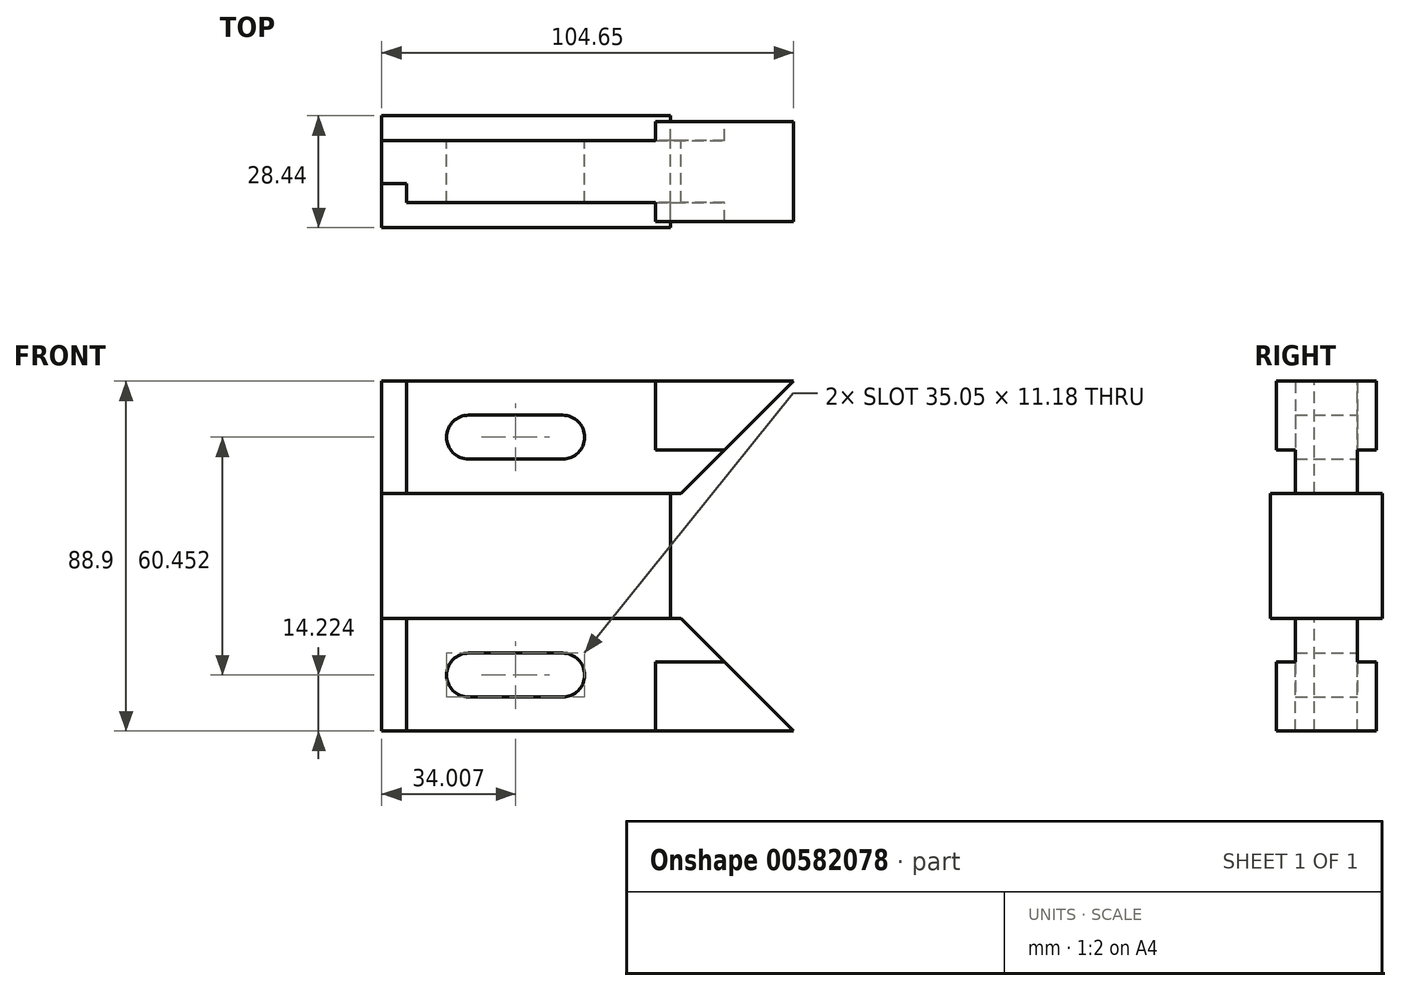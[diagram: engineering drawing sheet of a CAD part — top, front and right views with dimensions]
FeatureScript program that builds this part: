
annotation { "Feature Type Name" : "Feature", "Feature Type Description" : "" }
export const myFeature = defineFeature(function(context is Context, id is Id, definition is map)
    precondition{}
    {
        {
            var Q0;
            Q0=qCreatedBy(makeId("Front.planeOp"),FACE);
            var sketch = newSketch(context, id + "F0", { "sketchPlane" : qUnion([Q0])});
            skLineSegment(sketch, "E0", {"start": v(0, 0) * mm, "end": v(104.65, 0) * mm});
            skLineSegment(sketch, "E1", {"start": v(0, 0) * mm, "end": v(0, 88.9) * mm});
            skLineSegment(sketch, "E2", {"start": v(0, 28.58) * mm, "end": v(73.4, 28.58) * mm});
            skLineSegment(sketch, "E3", {"start": v(0, 60.33) * mm, "end": v(73.4, 60.33) * mm});
            skLineSegment(sketch, "E4", {"start": v(73.4, 60.33) * mm, "end": v(73.4, 28.58) * mm});
            skLineSegment(sketch, "E5", {"start": v(0, 88.9) * mm, "end": v(104.65, 88.9) * mm});
            skLineSegment(sketch, "E6", {"start": v(6.35, 88.9) * mm, "end": v(6.35, 60.33) * mm});
            skLineSegment(sketch, "E7", {"start": v(6.35, 0) * mm, "end": v(6.35, 28.58) * mm});
            skLineSegment(sketch, "E8", {"start": v(104.65, 0) * mm, "end": v(76.07, 28.58) * mm});
            skLineSegment(sketch, "E9", {"start": v(76.07, 28.58) * mm, "end": v(73.4, 28.58) * mm});
            skLineSegment(sketch, "E10", {"start": v(104.65, 88.9) * mm, "end": v(76.07, 60.32) * mm});
            skLineSegment(sketch, "E11", {"start": v(76.07, 60.33) * mm, "end": v(73.4, 60.33) * mm});
            skLineSegment(sketch, "E12", {"start": v(69.6, 88.9) * mm, "end": v(69.6, 71.37) * mm});
            skLineSegment(sketch, "E13", {"start": v(69.6, 71.37) * mm, "end": v(87.12, 71.37) * mm});
            skLineSegment(sketch, "E14", {"start": v(69.6, 0) * mm, "end": v(69.6, 17.53) * mm});
            skLineSegment(sketch, "E15", {"start": v(69.6, 17.53) * mm, "end": v(87.12, 17.53) * mm});
            skArc(sketch, "E16", {"start": v(22.07, 19.81) * mm, "mid": v(16.48, 14.22) * mm, "end": v(22.07, 8.64) * mm});
            skArc(sketch, "E17", {"start": v(45.95, 8.64) * mm, "mid": v(51.53, 14.22) * mm, "end": v(45.95, 19.81) * mm});
            skLineSegment(sketch, "E18", {"start": v(22.07, 19.81) * mm, "end": v(45.95, 19.81) * mm});
            skLineSegment(sketch, "E19", {"start": v(45.95, 8.64) * mm, "end": v(22.07, 8.64) * mm});
            skLineSegment(sketch, "E20", {"start": v(0, 44.45) * mm, "end": v(73.4, 44.45) * mm, "construction": true});
            skArc(sketch, "E21.MirrorCS", {"start": v(22.07, 69.09) * mm, "mid": v(16.48, 74.68) * mm, "end": v(22.07, 80.26) * mm});
            skLineSegment(sketch, "E22.MirrorCS", {"start": v(22.07, 69.09) * mm, "end": v(45.95, 69.09) * mm});
            skLineSegment(sketch, "E23.MirrorCS", {"start": v(45.95, 80.26) * mm, "end": v(22.07, 80.26) * mm});
            skArc(sketch, "E24.MirrorCS", {"start": v(45.95, 80.26) * mm, "mid": v(51.53, 74.68) * mm, "end": v(45.95, 69.09) * mm});
            skSolve(sketch);
        }
        {
            var Q0;
            {var subQ4=sQuery(id+"F0.wireOp",EDGE,"E4");Q0=makeQuery(id+"F0.imprint","IMPRINT",FACE,{"disambiguationData":[TD([[makeQuery(id+"F0.imprint","IMPRINT",EDGE,{"derivedFrom":subQ4}),-1.0]])]});}
            extrude(context, id + "F1", {"entities" : qUnion([Q0]), "endBound" : BoundingType.SYMMETRIC, "depth" : 28.45 * mm, "offsetDistance" : 25.4 * mm});
        }
        {
            var Q0;
            {var subQ3=sQuery(id+"F0.wireOp",EDGE,"E6");Q0=makeQuery(id+"F0.imprint","IMPRINT",FACE,{"disambiguationData":[TD([[makeQuery(id+"F0.imprint","IMPRINT",EDGE,{"derivedFrom":subQ3}),1.0]])]});}
            var Q1;
            {var subQ2=sQuery(id+"F0.wireOp",EDGE,"E7");Q1=makeQuery(id+"F0.imprint","IMPRINT",FACE,{"disambiguationData":[TD([[makeQuery(id+"F0.imprint","IMPRINT",EDGE,{"derivedFrom":subQ2}),-1.0]])]});}
            var Q2;
            {var subQ5=sQuery(id+"F0.wireOp",EDGE,"E6");Q2=makeQuery(id+"F0.imprint","IMPRINT",FACE,{"disambiguationData":[TD([[makeQuery(id+"F0.imprint","IMPRINT",EDGE,{"derivedFrom":subQ5}),-1.0]])]});}
            var Q3;
            {var subQ3=sQuery(id+"F0.wireOp",EDGE,"E7");Q3=makeQuery(id+"F0.imprint","IMPRINT",FACE,{"disambiguationData":[TD([[makeQuery(id+"F0.imprint","IMPRINT",EDGE,{"derivedFrom":subQ3}),1.0]])]});}
            extrude(context, id + "F2", {"entities" : qUnion([Q0, Q1, Q2, Q3]), "operationType" : NewBodyOperationType.ADD, "endBound" : BoundingType.SYMMETRIC, "depth" : 15.75 * mm, "offsetDistance" : 25.4 * mm});
        }
        {
            var Q0;
            {var subQ3=sQuery(id+"F0.wireOp",EDGE,"E12");Q0=makeQuery(id+"F0.imprint","IMPRINT",FACE,{"disambiguationData":[TD([[makeQuery(id+"F0.imprint","IMPRINT",EDGE,{"derivedFrom":subQ3}),1.0]])]});}
            var Q1;
            {var subQ3=sQuery(id+"F0.wireOp",EDGE,"E14");Q1=makeQuery(id+"F0.imprint","IMPRINT",FACE,{"disambiguationData":[TD([[makeQuery(id+"F0.imprint","IMPRINT",EDGE,{"derivedFrom":subQ3}),-1.0]])]});}
            extrude(context, id + "F3", {"entities" : qUnion([Q0, Q1]), "operationType" : NewBodyOperationType.ADD, "endBound" : BoundingType.SYMMETRIC, "depth" : 25.4 * mm, "offsetDistance" : 25.4 * mm});
        }
        {
            var Q0;
            Q0=makeQuery(id+"F2.opExtrude","CAP_FACE",FACE,{"disambiguationData":[OSD([sQuery(id+"F0.wireOp",EDGE,"E1"),sQuery(id+"F0.wireOp",EDGE,"E3"),sQuery(id+"F0.wireOp",EDGE,"E5"),sQuery(id+"F0.wireOp",EDGE,"E10"),sQuery(id+"F0.wireOp",EDGE,"E11"),sQuery(id+"F0.wireOp",EDGE,"E12"),sQuery(id+"F0.wireOp",EDGE,"E13"),sQuery(id+"F0.wireOp",EDGE,"E21.MirrorCS"),sQuery(id+"F0.wireOp",EDGE,"E22.MirrorCS"),sQuery(id+"F0.wireOp",EDGE,"E23.MirrorCS"),sQuery(id+"F0.wireOp",EDGE,"E24.MirrorCS")])],"isStart":false});
            var sketch = newSketch(context, id + "F4", { "sketchPlane" : qUnion([Q0])});
            skLineSegment(sketch, "E25.0", {"start": v(6.35, 88.9) * mm, "end": v(6.35, 60.33) * mm});
            skLineSegment(sketch, "E26.0", {"start": v(0, 0) * mm, "end": v(0, 88.9) * mm});
            skLineSegment(sketch, "E27.0", {"start": v(6.35, 0) * mm, "end": v(6.35, 28.58) * mm});
            skLineSegment(sketch, "E28.0", {"start": v(0, 0) * mm, "end": v(6.35, 0) * mm});
            skLineSegment(sketch, "E29.0", {"start": v(0, 28.58) * mm, "end": v(6.35, 28.58) * mm});
            skLineSegment(sketch, "E30.0", {"start": v(0, 88.9) * mm, "end": v(6.35, 88.9) * mm});
            skPoint(sketch, "E31.orphan", {"position": v(104.65, 88.9) * mm});
            skPoint(sketch, "E32.orphan", {"position": v(69.6, 0) * mm});
            skPoint(sketch, "E33.orphan", {"position": v(73.4, 28.58) * mm});
            skLineSegment(sketch, "E34.0", {"start": v(6.35, 60.32) * mm, "end": v(0, 60.32) * mm});
            skPoint(sketch, "E35.orphan", {"position": v(73.4, 60.33) * mm});
            skSolve(sketch);
        }
        {
            var Q0;
            Q0=makeQuery(id+"F4.imprint","IMPRINT",FACE,{"disambiguationData":[TD([[makeQuery(id+"F4.imprint","IMPRINT",EDGE,{"derivedFrom":sQuery(id+"F4.wireOp",EDGE,"E25.0")}),-1.0]])]});
            var Q1;
            Q1=makeQuery(id+"F4.imprint","IMPRINT",FACE,{"disambiguationData":[TD([[makeQuery(id+"F4.imprint","IMPRINT",EDGE,{"derivedFrom":sQuery(id+"F4.wireOp",EDGE,"E27.0")}),1.0]])]});
            extrude(context, id + "F5", {"entities" : qUnion([Q0, Q1]), "operationType" : NewBodyOperationType.REMOVE, "oppositeDirection" : true, "depth" : 4.83 * mm, "offsetDistance" : 25.4 * mm});
        }
    });
